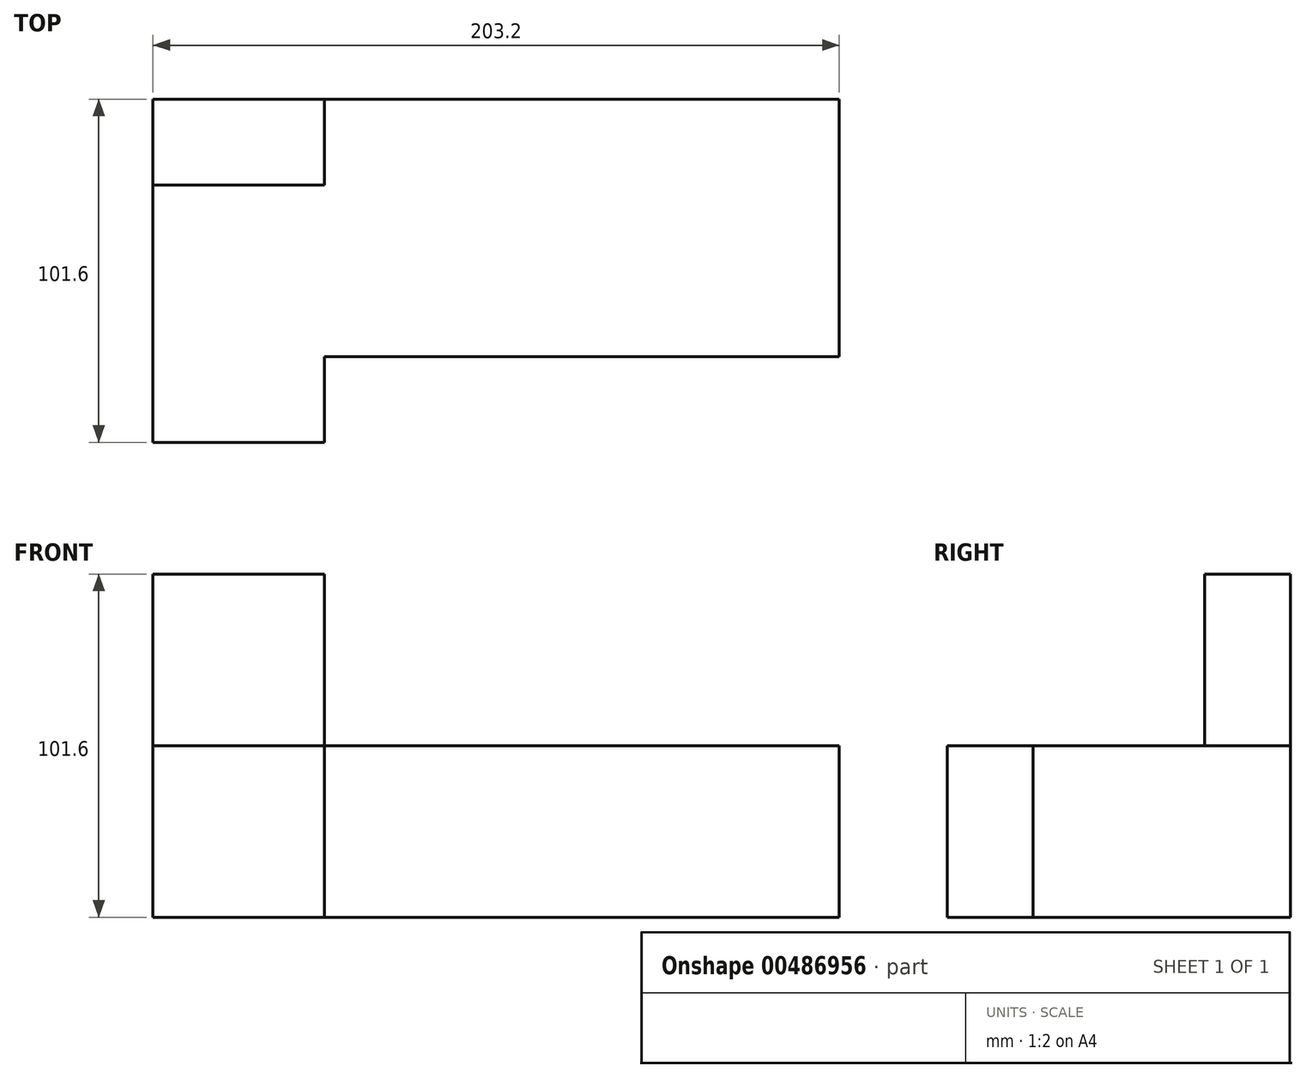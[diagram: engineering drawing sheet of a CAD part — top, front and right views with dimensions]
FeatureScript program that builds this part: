
annotation { "Feature Type Name" : "Feature", "Feature Type Description" : "" }
export const myFeature = defineFeature(function(context is Context, id is Id, definition is map)
    precondition{}
    {
        {
            var Q0;
            Q0=qCreatedBy(makeId("Top.planeOp"),FACE);
            var sketch = newSketch(context, id + "F0", { "sketchPlane" : qUnion([Q0])});
            skLineSegment(sketch, "E0.bottom", {"start": v(-123.33, 79.78) * mm, "end": v(79.87, 79.78) * mm});
            skLineSegment(sketch, "E0.top", {"start": v(-123.33, -21.82) * mm, "end": v(79.87, -21.82) * mm});
            skLineSegment(sketch, "E0.left", {"start": v(-123.33, 79.78) * mm, "end": v(-123.33, -21.82) * mm});
            skLineSegment(sketch, "E0.right", {"start": v(79.87, 79.78) * mm, "end": v(79.87, -21.82) * mm});
            skSolve(sketch);
        }
        {
            var Q0;
            Q0 = qSketchRegion(id + "F0", true);
            extrude(context, id + "F1", {"entities" : qUnion([Q0]), "depth" : 50.8 * mm});
        }
        {
            var Q0;
            Q0=makeQuery(id+"F1.opExtrude","CAP_FACE",FACE,{"disambiguationData":[OSD([sQuery(id+"F0.wireOp",EDGE,"E0.bottom"),sQuery(id+"F0.wireOp",EDGE,"E0.top"),sQuery(id+"F0.wireOp",EDGE,"E0.left"),sQuery(id+"F0.wireOp",EDGE,"E0.right")])],"isStart":false});
            var sketch = newSketch(context, id + "F2", { "sketchPlane" : qUnion([Q0])});
            skLineSegment(sketch, "E1.bottom", {"start": v(79.87, -21.82) * mm, "end": v(-72.53, -21.82) * mm});
            skLineSegment(sketch, "E1.top", {"start": v(79.87, 3.58) * mm, "end": v(-72.53, 3.58) * mm});
            skLineSegment(sketch, "E1.left", {"start": v(79.87, -21.82) * mm, "end": v(79.87, 3.58) * mm});
            skLineSegment(sketch, "E1.right", {"start": v(-72.53, -21.82) * mm, "end": v(-72.53, 3.58) * mm});
            skLineSegment(sketch, "E2.bottom", {"start": v(-123.33, 79.78) * mm, "end": v(-72.53, 79.78) * mm});
            skLineSegment(sketch, "E2.top", {"start": v(-123.33, 54.38) * mm, "end": v(-72.53, 54.38) * mm});
            skLineSegment(sketch, "E2.left", {"start": v(-123.33, 79.78) * mm, "end": v(-123.33, 54.38) * mm});
            skLineSegment(sketch, "E2.right", {"start": v(-72.53, 79.78) * mm, "end": v(-72.53, 54.38) * mm});
            skSolve(sketch);
        }
        {
            var Q0;
            Q0=makeQuery(id+"F2.imprint","IMPRINT",FACE,{"disambiguationData":[TD([[makeQuery(id+"F2.imprint","IMPRINT",EDGE,{"derivedFrom":sQuery(id+"F2.wireOp",EDGE,"E2.bottom")}),-1.0]])]});
            extrude(context, id + "F3", {"entities" : qUnion([Q0]), "operationType" : NewBodyOperationType.ADD, "depth" : 50.8 * mm});
        }
        {
            var Q0;
            Q0=makeQuery(id+"F2.imprint","IMPRINT",FACE,{"disambiguationData":[TD([[makeQuery(id+"F2.imprint","IMPRINT",EDGE,{"derivedFrom":sQuery(id+"F2.wireOp",EDGE,"E1.bottom")}),1.0]])]});
            extrude(context, id + "F4", {"entities" : qUnion([Q0]), "operationType" : NewBodyOperationType.REMOVE, "oppositeDirection" : true, "depth" : 50.8 * mm});
        }
    });
